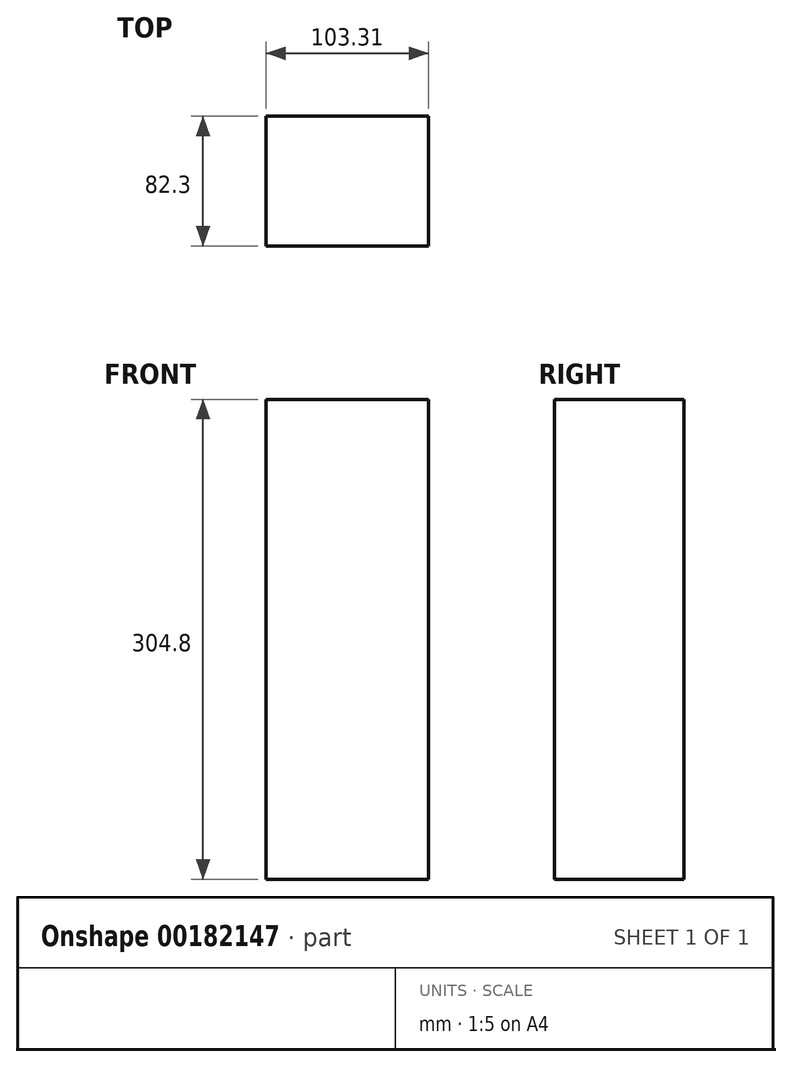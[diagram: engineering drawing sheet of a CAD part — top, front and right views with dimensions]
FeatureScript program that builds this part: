
annotation { "Feature Type Name" : "Feature", "Feature Type Description" : "" }
export const myFeature = defineFeature(function(context is Context, id is Id, definition is map)
    precondition{}
    {
        {
            assignVariable(context, id + "F0", {"name" : "Jo", "anyValue" : 304.8 * mm});
        }
        {
            var Q0;
            Q0=qCreatedBy(makeId("Top.planeOp"),FACE);
            var sketch = newSketch(context, id + "F1", { "sketchPlane" : qUnion([Q0])});
            skLineSegment(sketch, "E0.bottom", {"start": v(-49.65, -37.93) * mm, "end": v(53.66, -37.93) * mm});
            skLineSegment(sketch, "E0.top", {"start": v(-49.65, 44.37) * mm, "end": v(53.66, 44.37) * mm});
            skLineSegment(sketch, "E0.left", {"start": v(-49.65, -37.93) * mm, "end": v(-49.65, 44.37) * mm});
            skLineSegment(sketch, "E0.right", {"start": v(53.66, -37.93) * mm, "end": v(53.66, 44.37) * mm});
            skSolve(sketch);
        }
        {
            var Q0;
            Q0=makeQuery(id+"F1.imprint","IMPRINT",FACE,{"disambiguationData":[TD([[makeQuery(id+"F1.imprint","IMPRINT",EDGE,{"derivedFrom":sQuery(id+"F1.wireOp",EDGE,"E0.bottom")}),1.0]])]});
            extrude(context, id + "F2", {"entities" : qUnion([Q0]), "depth" : getVariable(context, 'Jo')});
        }
    });
